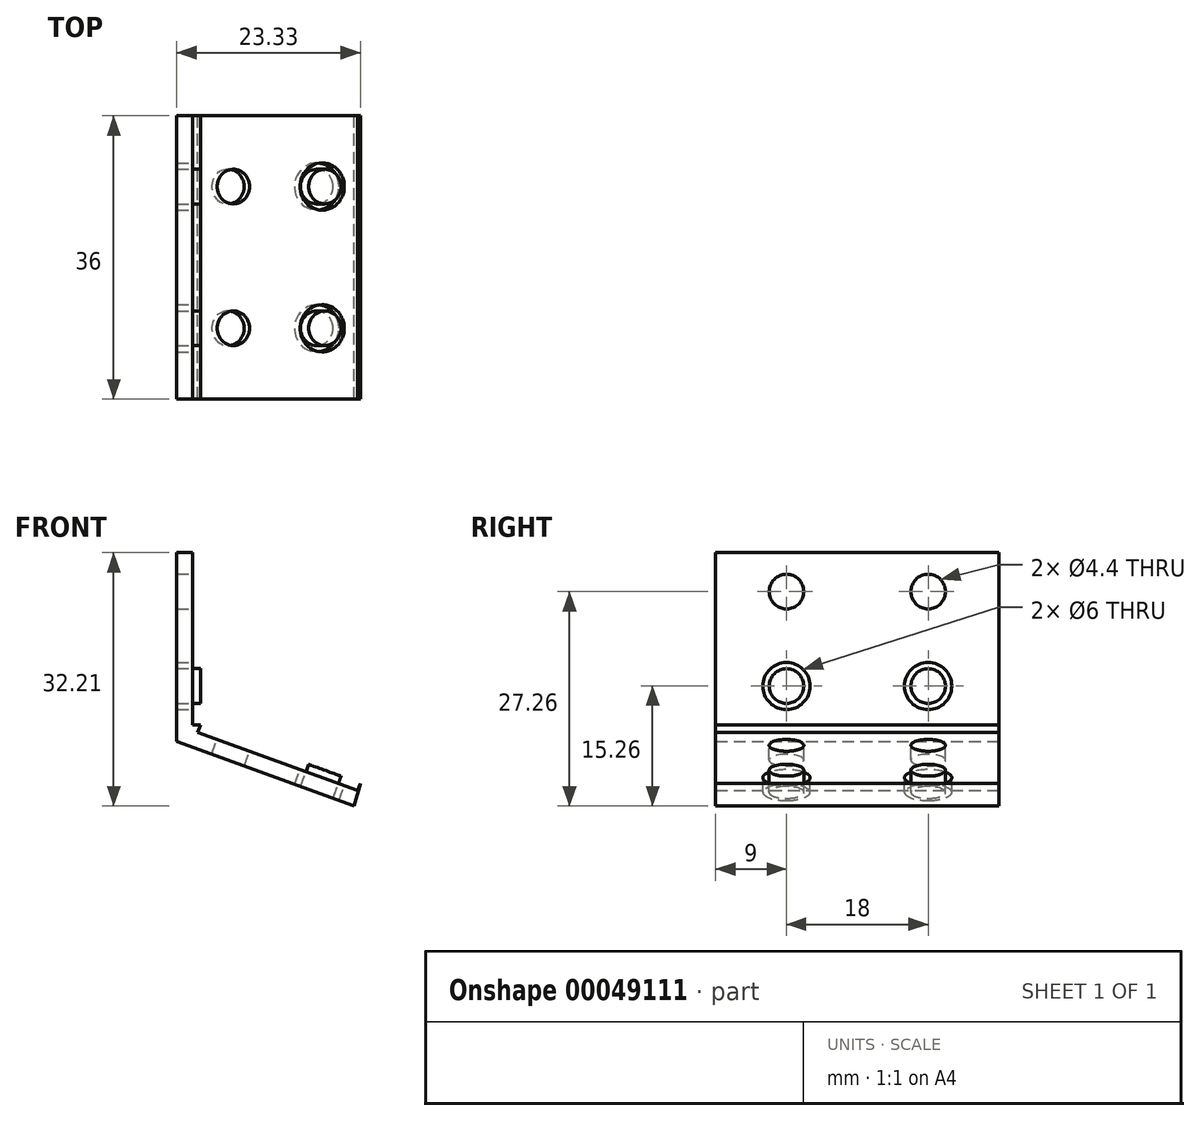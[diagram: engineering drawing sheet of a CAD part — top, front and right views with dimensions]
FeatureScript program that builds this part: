
annotation { "Feature Type Name" : "Feature", "Feature Type Description" : "" }
export const myFeature = defineFeature(function(context is Context, id is Id, definition is map)
    precondition{}
    {
        {
            var Q0;
            Q0=qCreatedBy(makeId("Front.planeOp"),FACE);
            var sketch = newSketch(context, id + "F0", { "sketchPlane" : qUnion([Q0])});
            skLineSegment(sketch, "E0", {"start": v(0, 0) * mm, "end": v(0, 24) * mm});
            skLineSegment(sketch, "E1", {"start": v(0, 0) * mm, "end": v(22.55, -8.2) * mm});
            skLineSegment(sketch, "E2.0", {"start": v(3, 2.1) * mm, "end": v(3, 24) * mm});
            skLineSegment(sketch, "E2.1", {"start": v(3, 2.1) * mm, "end": v(23.33, -5.3) * mm});
            skLineSegment(sketch, "E3", {"start": v(0, 24) * mm, "end": v(3, 24) * mm});
            skLineSegment(sketch, "E4", {"start": v(22.55, -8.2) * mm, "end": v(23.33, -5.3) * mm});
            skSolve(sketch);
        }
        {
            var Q0;
            Q0=makeQuery(id+"F0.imprint","IMPRINT",FACE,{"disambiguationData":[TD([[makeQuery(id+"F0.imprint","IMPRINT",EDGE,{"derivedFrom":sQuery(id+"F0.wireOp",EDGE,"E0")}),-1.0]])]});
            extrude(context, id + "F1", {"entities" : qUnion([Q0]), "depth" : 36 * mm});
        }
        {
            var Q0;
            Q0=makeQuery(id+"F1.opExtrude","SWEPT_FACE",FACE,{"disambiguationData":[OSD([sQuery(id+"F0.wireOp",EDGE,"E2.0")])]});
            var sketch = newSketch(context, id + "F2", { "sketchPlane" : qUnion([Q0])});
            skLineSegment(sketch, "E5", {"start": v(-36, 13.05) * mm, "end": v(0, 13.05) * mm, "construction": true});
            skLineSegment(sketch, "E6", {"start": v(-36, 19.05) * mm, "end": v(0, 19.05) * mm, "construction": true});
            skCircle(sketch, "E7", {"center": v(-27, 19.05) * mm, "radius": 3 * mm});
            skCircle(sketch, "E8", {"center": v(-9, 19.05) * mm, "radius": 3 * mm});
            skCircle(sketch, "E9", {"center": v(-27, 19.05) * mm, "radius": 2.2 * mm});
            skCircle(sketch, "E10", {"center": v(-9, 19.05) * mm, "radius": 2.2 * mm});
            skCircle(sketch, "E11.MirrorC", {"center": v(-27, 7.05) * mm, "radius": 3 * mm});
            skCircle(sketch, "E12.MirrorC", {"center": v(-27, 7.05) * mm, "radius": 2.2 * mm});
            skCircle(sketch, "E13.MirrorC", {"center": v(-9, 7.05) * mm, "radius": 3 * mm});
            skCircle(sketch, "E14.MirrorC", {"center": v(-9, 7.05) * mm, "radius": 2.2 * mm});
            skSolve(sketch);
        }
        {
            var Q0;
            Q0=makeQuery(id+"F1.opExtrude","SWEPT_FACE",FACE,{"disambiguationData":[OSD([sQuery(id+"F0.wireOp",EDGE,"E2.1")])]});
            var sketch = newSketch(context, id + "F3", { "sketchPlane" : qUnion([Q0])});
            skLineSegment(sketch, "E15", {"start": v(12.92, -36) * mm, "end": v(12.92, 0) * mm, "construction": true});
            skLineSegment(sketch, "E16", {"start": v(6.92, -36) * mm, "end": v(6.92, 0) * mm, "construction": true});
            skCircle(sketch, "E17", {"center": v(6.92, -27) * mm, "radius": 3 * mm});
            skCircle(sketch, "E18", {"center": v(6.92, -27) * mm, "radius": 2.2 * mm});
            skCircle(sketch, "E19", {"center": v(6.92, -9) * mm, "radius": 3 * mm});
            skCircle(sketch, "E20", {"center": v(6.92, -9) * mm, "radius": 2.2 * mm});
            skCircle(sketch, "E21.MirrorC", {"center": v(18.92, -27) * mm, "radius": 3 * mm});
            skCircle(sketch, "E22.MirrorC", {"center": v(18.92, -27) * mm, "radius": 2.2 * mm});
            skCircle(sketch, "E23.MirrorC", {"center": v(18.92, -9) * mm, "radius": 3 * mm});
            skCircle(sketch, "E24.MirrorC", {"center": v(18.92, -9) * mm, "radius": 2.2 * mm});
            skSolve(sketch);
        }
        {
            var Q0;
            Q0=makeQuery(id+"F2.imprint","IMPRINT",FACE,{"disambiguationData":[TD([[makeQuery(id+"F2.imprint","IMPRINT",EDGE,{"derivedFrom":sQuery(id+"F2.wireOp",EDGE,"E9")}),1.0]])]});
            var Q1;
            Q1=makeQuery(id+"F2.imprint","IMPRINT",FACE,{"disambiguationData":[TD([[makeQuery(id+"F2.imprint","IMPRINT",EDGE,{"derivedFrom":sQuery(id+"F2.wireOp",EDGE,"E12.MirrorC")}),-1.0]])]});
            var Q2;
            Q2=makeQuery(id+"F2.imprint","IMPRINT",FACE,{"disambiguationData":[TD([[makeQuery(id+"F2.imprint","IMPRINT",EDGE,{"derivedFrom":sQuery(id+"F2.wireOp",EDGE,"E14.MirrorC")}),-1.0]])]});
            var Q3;
            Q3=makeQuery(id+"F2.imprint","IMPRINT",FACE,{"disambiguationData":[TD([[makeQuery(id+"F2.imprint","IMPRINT",EDGE,{"derivedFrom":sQuery(id+"F2.wireOp",EDGE,"E10")}),1.0]])]});
            extrude(context, id + "F4", {"entities" : qUnion([Q0, Q1, Q2, Q3]), "operationType" : NewBodyOperationType.REMOVE, "endBound" : BoundingType.THROUGH_ALL, "oppositeDirection" : true, "depth" : 25 * mm});
        }
        {
            var Q0;
            Q0=makeQuery(id+"F3.imprint","IMPRINT",FACE,{"disambiguationData":[TD([[makeQuery(id+"F3.imprint","IMPRINT",EDGE,{"derivedFrom":sQuery(id+"F3.wireOp",EDGE,"E18")}),1.0]])]});
            var Q1;
            Q1=makeQuery(id+"F3.imprint","IMPRINT",FACE,{"disambiguationData":[TD([[makeQuery(id+"F3.imprint","IMPRINT",EDGE,{"derivedFrom":sQuery(id+"F3.wireOp",EDGE,"E22.MirrorC")}),-1.0]])]});
            var Q2;
            Q2=makeQuery(id+"F3.imprint","IMPRINT",FACE,{"disambiguationData":[TD([[makeQuery(id+"F3.imprint","IMPRINT",EDGE,{"derivedFrom":sQuery(id+"F3.wireOp",EDGE,"E20")}),1.0]])]});
            var Q3;
            Q3=makeQuery(id+"F3.imprint","IMPRINT",FACE,{"disambiguationData":[TD([[makeQuery(id+"F3.imprint","IMPRINT",EDGE,{"derivedFrom":sQuery(id+"F3.wireOp",EDGE,"E24.MirrorC")}),-1.0]])]});
            extrude(context, id + "F5", {"entities" : qUnion([Q0, Q1, Q2, Q3]), "operationType" : NewBodyOperationType.REMOVE, "endBound" : BoundingType.THROUGH_ALL, "oppositeDirection" : true, "depth" : 25 * mm});
        }
        {
            var Q0;
            Q0=makeQuery(id+"F3.imprint","IMPRINT",FACE,{"disambiguationData":[TD([[makeQuery(id+"F3.imprint","IMPRINT",EDGE,{"derivedFrom":sQuery(id+"F3.wireOp",EDGE,"E17")}),1.0]])]});
            var Q1;
            Q1=makeQuery(id+"F3.imprint","IMPRINT",FACE,{"disambiguationData":[TD([[makeQuery(id+"F3.imprint","IMPRINT",EDGE,{"derivedFrom":sQuery(id+"F3.wireOp",EDGE,"E21.MirrorC")}),-1.0]])]});
            var Q2;
            Q2=makeQuery(id+"F3.imprint","IMPRINT",FACE,{"disambiguationData":[TD([[makeQuery(id+"F3.imprint","IMPRINT",EDGE,{"derivedFrom":sQuery(id+"F3.wireOp",EDGE,"E23.MirrorC")}),-1.0]])]});
            var Q3;
            Q3=makeQuery(id+"F3.imprint","IMPRINT",FACE,{"disambiguationData":[TD([[makeQuery(id+"F3.imprint","IMPRINT",EDGE,{"derivedFrom":sQuery(id+"F3.wireOp",EDGE,"E19")}),1.0]])]});
            extrude(context, id + "F6", {"entities" : qUnion([Q0, Q1, Q2, Q3]), "operationType" : NewBodyOperationType.REMOVE, "oppositeDirection" : true, "depth" : 1 * mm});
        }
        {
            var Q0;
            Q0=makeQuery(id+"F2.imprint","IMPRINT",FACE,{"disambiguationData":[TD([[makeQuery(id+"F2.imprint","IMPRINT",EDGE,{"derivedFrom":sQuery(id+"F2.wireOp",EDGE,"E7")}),1.0]])]});
            var Q1;
            Q1=makeQuery(id+"F2.imprint","IMPRINT",FACE,{"disambiguationData":[TD([[makeQuery(id+"F2.imprint","IMPRINT",EDGE,{"derivedFrom":sQuery(id+"F2.wireOp",EDGE,"E13.MirrorC")}),-1.0]])]});
            var Q2;
            Q2=makeQuery(id+"F2.imprint","IMPRINT",FACE,{"disambiguationData":[TD([[makeQuery(id+"F2.imprint","IMPRINT",EDGE,{"derivedFrom":sQuery(id+"F2.wireOp",EDGE,"E8")}),1.0]])]});
            var Q3;
            Q3=makeQuery(id+"F2.imprint","IMPRINT",FACE,{"disambiguationData":[TD([[makeQuery(id+"F2.imprint","IMPRINT",EDGE,{"derivedFrom":sQuery(id+"F2.wireOp",EDGE,"E11.MirrorC")}),-1.0]])]});
            extrude(context, id + "F7", {"entities" : qUnion([Q0, Q1, Q2, Q3]), "operationType" : NewBodyOperationType.REMOVE, "oppositeDirection" : true, "depth" : 1 * mm});
        }
    });
